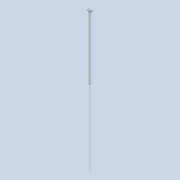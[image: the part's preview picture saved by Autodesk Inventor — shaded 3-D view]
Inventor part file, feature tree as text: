
AUTODESK INVENTOR PART (.ipt)
format: ipt  version: 2020 (Build 240168000, 168)  size: 84,992 bytes
history: native  units: mm
features: extrude x3, sketch x3
ambient origin geometry x8: Origin, YZ Plane, XZ Plane, XY Plane, X Axis, Y Axis, Z Axis, Center Point
bodies: Solid1 (feature_tree)
feature tree (6):
  extrude  "Extrusion1"  Depth=40.0mm TaperAngle=0.0deg
  extrude  "Extrusion2"  Depth=33.0mm TaperAngle=0.0deg
  extrude  "Extrusion3"  Depth=1.4mm
  sketch  "Sketch1"  dims[d0=0.3mm d1=40.0mm d2=0.0mm]
  sketch  "Sketch2"  dims[d3=1.0mm d4=33.0mm d5=0.0mm]
  sketch  "Sketch3"  dims[d6=0.4mm d7=1.0mm d8=1.4mm d9=0.0mm]
